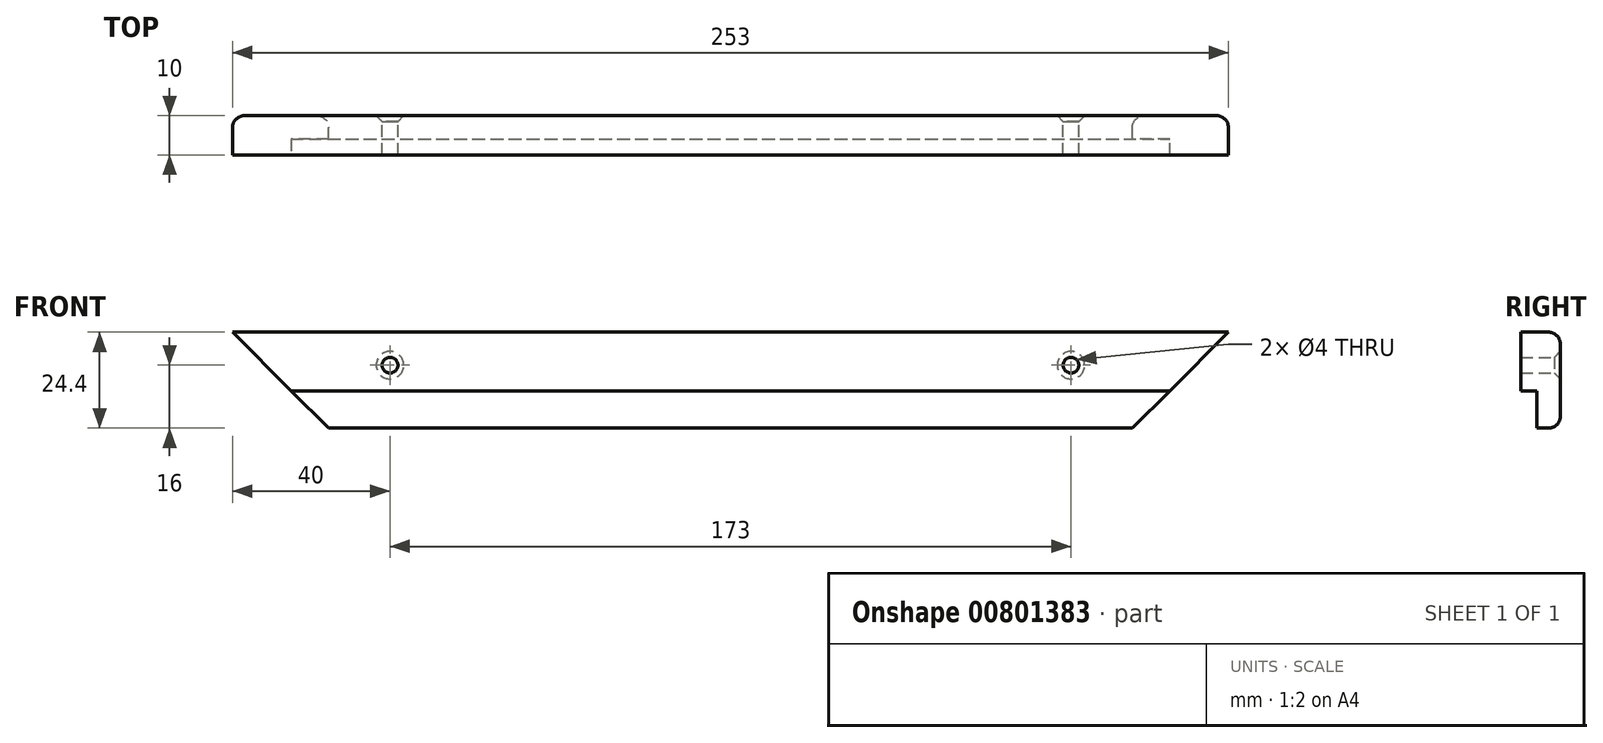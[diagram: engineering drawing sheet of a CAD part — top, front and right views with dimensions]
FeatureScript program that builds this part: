
annotation { "Feature Type Name" : "Feature", "Feature Type Description" : "" }
export const myFeature = defineFeature(function(context is Context, id is Id, definition is map)
    precondition{}
    {
        {
            var Q0;
            Q0=qCreatedBy(makeId("Front.planeOp"),FACE);
            var sketch = newSketch(context, id + "F0", { "sketchPlane" : qUnion([Q0])});
            skLineSegment(sketch, "E0", {"start": v(-24.4, 24.4) * mm, "end": v(228.6, 24.4) * mm});
            skLineSegment(sketch, "E1", {"start": v(228.6, 24.4) * mm, "end": v(204.2, 0) * mm});
            skLineSegment(sketch, "E2", {"start": v(204.2, 0) * mm, "end": v(0, 0) * mm});
            skLineSegment(sketch, "E3", {"start": v(0, 0) * mm, "end": v(-24.4, 24.4) * mm});
            skSolve(sketch);
        }
        {
            var Q0;
            Q0=makeQuery(id+"F0.imprint","IMPRINT",FACE,{"disambiguationData":[TD([[makeQuery(id+"F0.imprint","IMPRINT",EDGE,{"derivedFrom":sQuery(id+"F0.wireOp",EDGE,"E0")}),-1.0]])]});
            extrude(context, id + "F1", {"entities" : qUnion([Q0]), "depth" : 10 * mm, "offsetDistance" : 25 * mm});
        }
        {
            var Q0;
            Q0=makeQuery(id+"F1.opExtrude","CAP_FACE",FACE,{"disambiguationData":[OSD([sQuery(id+"F0.wireOp",EDGE,"E0"),sQuery(id+"F0.wireOp",EDGE,"E1"),sQuery(id+"F0.wireOp",EDGE,"E2"),sQuery(id+"F0.wireOp",EDGE,"E3")])],"isStart":false});
            var sketch = newSketch(context, id + "F2", { "sketchPlane" : qUnion([Q0])});
            skLineSegment(sketch, "E4.bottom", {"start": v(-24.4, 0) * mm, "end": v(228.6, 0) * mm});
            skLineSegment(sketch, "E4.top", {"start": v(-24.4, 9.5) * mm, "end": v(228.6, 9.5) * mm});
            skLineSegment(sketch, "E4.left", {"start": v(-24.4, 0) * mm, "end": v(-24.4, 9.5) * mm});
            skLineSegment(sketch, "E4.right", {"start": v(228.6, 0) * mm, "end": v(228.6, 9.5) * mm});
            skSolve(sketch);
        }
        {
            var Q0;
            {var subQ3=sQuery(id+"F2.wireOp",EDGE,"E4.left");Q0=makeQuery(id+"F2.imprint","IMPRINT",FACE,{"disambiguationData":[TD([[makeQuery(id+"F2.imprint","IMPRINT",EDGE,{"derivedFrom":subQ3}),-1.0]])]});}
            var Q1;
            {var subQ0=sQuery(id+"F2.wireOp",EDGE,"E4.bottom");var subQ1=makeQuery(id+"F1.opExtrude","CAP_EDGE",EDGE,{"disambiguationData":[OSD([sQuery(id+"F0.wireOp",EDGE,"E1")])],"isStart":false});var subQ2=makeQuery(id+"F2.imprint","INTERSECT",VERTEX,{"derivedFrom":[subQ1,subQ0]});var subQ3=makeQuery(id+"F1.opExtrude","CAP_EDGE",EDGE,{"disambiguationData":[OSD([sQuery(id+"F0.wireOp",EDGE,"E3")])],"isStart":false});var subQ4=makeQuery(id+"F2.imprint","INTERSECT",VERTEX,{"derivedFrom":[subQ3,subQ0]});Q1=makeQuery(id+"F2.imprint","IMPRINT",FACE,{"disambiguationData":[TD([[makeQuery(id+"F2.imprint","IMPRINT",EDGE,{"disambiguationData":[TD([[subQ2,-1.0],[subQ4,1.0]])],"derivedFrom":subQ0}),-1.0]])]});}
            var Q2;
            {var subQ3=sQuery(id+"F2.wireOp",EDGE,"E4.right");Q2=makeQuery(id+"F2.imprint","IMPRINT",FACE,{"disambiguationData":[TD([[makeQuery(id+"F2.imprint","IMPRINT",EDGE,{"derivedFrom":subQ3}),1.0]])]});}
            extrude(context, id + "F3", {"entities" : qUnion([Q0, Q1, Q2]), "operationType" : NewBodyOperationType.REMOVE, "oppositeDirection" : true, "depth" : 4 * mm, "offsetDistance" : 25 * mm});
        }
        {
            var Q0;
            Q0=makeQuery(id+"F1.opExtrude","CAP_FACE",FACE,{"disambiguationData":[OSD([sQuery(id+"F0.wireOp",EDGE,"E0"),sQuery(id+"F0.wireOp",EDGE,"E1"),sQuery(id+"F0.wireOp",EDGE,"E2"),sQuery(id+"F0.wireOp",EDGE,"E3")])],"isStart":true});
            var sketch = newSketch(context, id + "F4", { "sketchPlane" : qUnion([Q0])});
            skLineSegment(sketch, "E5", {"start": v(-188.6, 16) * mm, "end": v(-15.6, 16) * mm});
            skLineSegment(sketch, "E6", {"start": v(-102.1, 16) * mm, "end": v(-102.1, 0) * mm, "construction": true});
            skSolve(sketch);
        }
        {
            var Q0;
            Q0=sQuery(id+"F4.wireOp",VERTEX,"E5.start");
            var Q1;
            Q1=sQuery(id+"F4.wireOp",VERTEX,"E5.end");
            var Q2;
            Q2=makeQuery(id+"F1.opExtrude","SWEPT_BODY",BODY,{"disambiguationData":[OSD([sQuery(id+"F0.wireOp",EDGE,"E0"),sQuery(id+"F0.wireOp",EDGE,"E1"),sQuery(id+"F0.wireOp",EDGE,"E2"),sQuery(id+"F0.wireOp",EDGE,"E3")])]});
            hole(context, id + "F5", {"style" : HoleStyle.C_SINK, "endStyle" : HoleEndStyle.THROUGH, "holeDiameter" : 4 * mm, "cSinkDiameter" : 7 * mm, "cSinkAngle" : 90 * degree, "majorDiameter" : 5 * mm, "isTappedThrough" : true, "tappedDepth" : 12 * mm, "tapClearance" : 3, "locations" : qUnion([Q0, Q1]), "scope" : qUnion([Q2])});
        }
        {
            var Q0;
            Q0=makeQuery(id+"F1.opExtrude","CAP_EDGE",EDGE,{"disambiguationData":[OSD([sQuery(id+"F0.wireOp",EDGE,"E2")])],"isStart":true});
            var Q1;
            Q1=makeQuery(id+"F1.opExtrude","CAP_EDGE",EDGE,{"disambiguationData":[OSD([sQuery(id+"F0.wireOp",EDGE,"E0")])],"isStart":true});
            fillet(context, id + "F6", {"entities" : qUnion([Q0, Q1]), "radius" : 3 * mm, "tangentPropagation" : true, "allowEdgeOverflow" : false});
        }
    });
